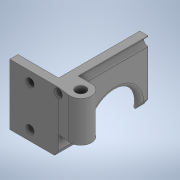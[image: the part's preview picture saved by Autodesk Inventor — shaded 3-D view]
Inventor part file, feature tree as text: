
AUTODESK INVENTOR PART (.ipt)
format: ipt  version: 2022 (Build 260153000, 153)  size: 258,048 bytes
history: native  units: mm
features: other x10, extrude x8, sketch x8, reference x5, projected_geometry x4, fillet x3, plane x1, chamfer x1
ambient origin geometry x8: Origin, YZ Plane, XZ Plane, XY Plane, X Axis, Y Axis, Z Axis, Center Point
bodies: Solid1 (feature_tree)
feature tree (40):
  extrude  "Extrusion1"  Depth=4.0mm
  plane  "Work Plane1"
  extrude  "Extrusion3"  Depth=5.0mm
  extrude  "Extrusion2"  Depth=4.0mm TaperAngle=0.0deg
  extrude  "Extrusion4"  Depth=10.0mm TaperAngle=0.0deg
  fillet  "Fillet1"  Radius=20.0mm
  extrude  "Extrusion5"  Depth=4.0mm
  fillet  "Fillet2"  Radius=5.0mm
  extrude  "Extrusion6"  Depth=4.0mm TaperAngle=0.0deg
  chamfer  "Chamfer1"  Distance=10.0mm
  extrude  "Extrusion7"  Depth=5.0mm
  extrude  "Extrusion8"  Depth=2.0mm
  fillet  "Fillet3"  Radius=6.5mm
  sketch  "Sketch1"  dims[d0=30.0mm d1=4.0mm]
  reference  "Reference1"
  reference  "Reference2"
  reference  "Reference3"
  sketch  "Sketch2"  dims[d2=4.0mm d3=5.0mm]
  sketch  "Sketch3"  dims[d4=5.0mm d5=4.0mm d6=0.0mm]
  projected_geometry  "Projected Loop1"
  projected_geometry  "Projected Loop2"
  sketch  "Sketch4"  dims[d7=-15.0mm d10=10.0mm d11=0.0mm d12=20.0mm]
  projected_geometry  "Projected Loop3"
  sketch  "Sketch5"  dims[d13=4.0mm d14=4.0mm d15=5.0mm]
  sketch  "Sketch6"  dims[d16=5.0mm d17=4.0mm d18=0.0mm d19=10.0mm d20=0.0mm]
  reference  "Reference7"
  reference  "Reference8"
  sketch  "Sketch7"  dims[d21=5.0mm d26=5.0mm]
  projected_geometry  "Projected Loop4"
  sketch  "Sketch8"  dims[d27=2.75mm d29=4.445584mm d30=6.5mm d36=30.0mm d37=0.0mm d38=2.0mm d39=6.5mm d40=20.0mm d41=2.0mm d42=4.2mm d43=2.5mm d44=4.0mm d45=100.0mm d46=0.0mm d47=3.0mm d48=2.0mm d49=45.0deg d50=10.5mm d51=20.0mm d52=0.0mm d53=5.0mm d54=2.5mm d55=24.0mm d56=7.75mm d57=23.55mm d58=10.0mm d59=0.0mm d60=2.0mm]
  parser-record x2  (decoder bookkeeping rows leaked as tree rows — omitted from the tree; the rows remain in map.json)
  other  "speedyPrinty.iam"
  other  "V-Slot 20x20x500 Linear Rail:1"
  other  "Motor Mount Right:2"
  other  "Y motor mount part B (top)(Mirror):1"
  other  "speedyPrinty_REAR TOOL.iam"
  other  "volcano tool:7"
  other  "4010 turbo fan v3:1"
  other  "4010 part cooling duct:1"
note: 2 file-system paths scrubbed to <path> (originals preserved in map.json)
